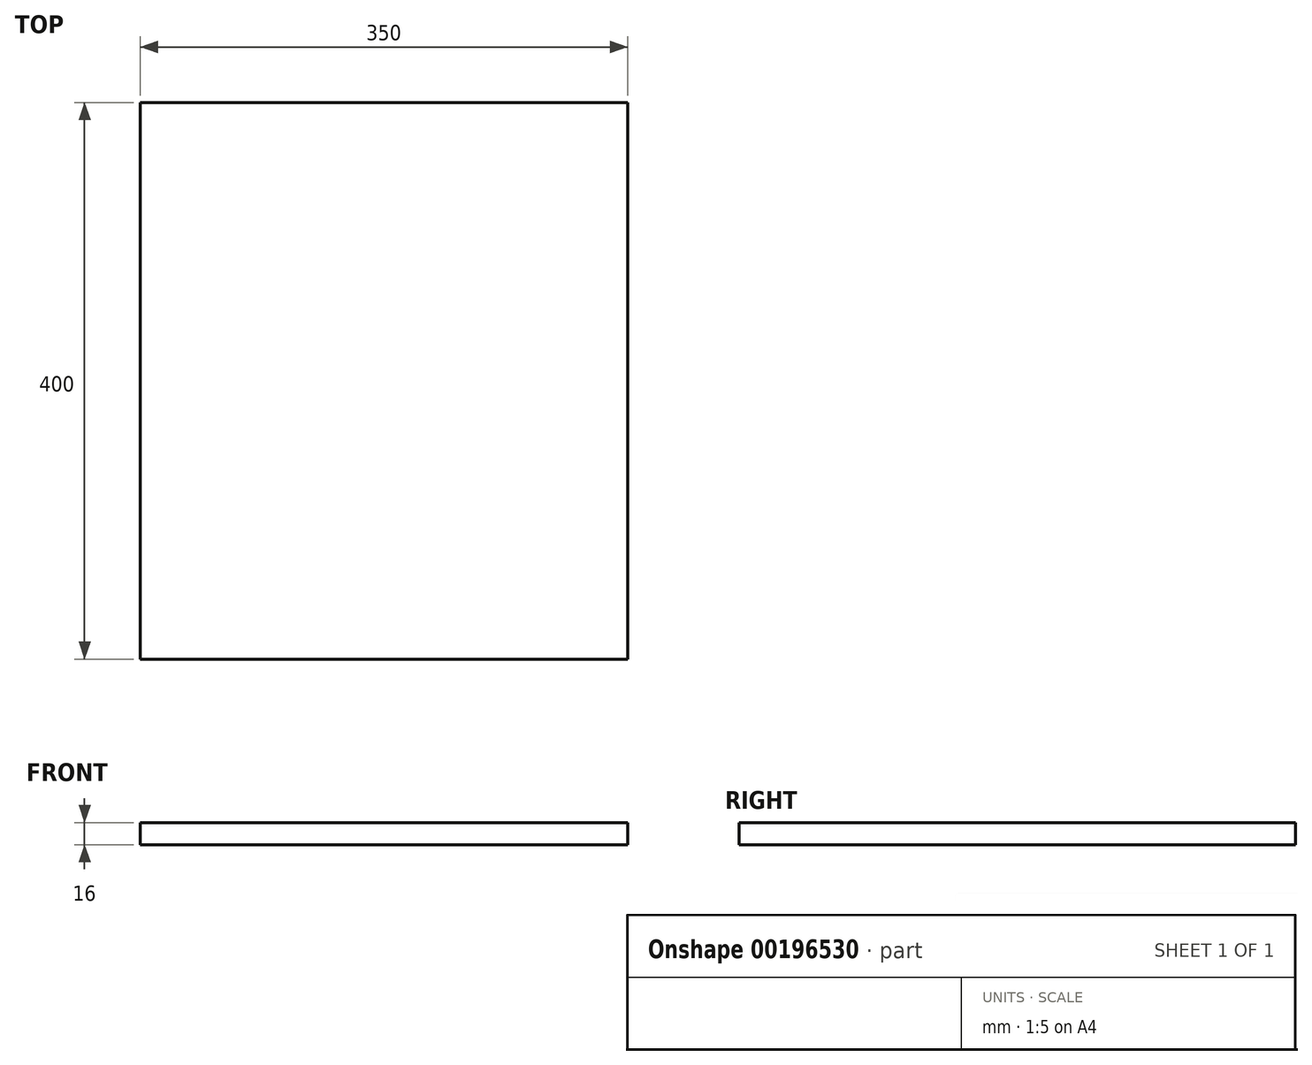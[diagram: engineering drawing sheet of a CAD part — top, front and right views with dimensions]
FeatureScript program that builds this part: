
annotation { "Feature Type Name" : "Feature", "Feature Type Description" : "" }
export const myFeature = defineFeature(function(context is Context, id is Id, definition is map)
    precondition{}
    {
        {
            var Q0;
            Q0=qCreatedBy(makeId("Top.planeOp"),FACE);
            var sketch = newSketch(context, id + "F0", { "sketchPlane" : qUnion([Q0])});
            skLineSegment(sketch, "E0.bottom", {"start": v(-864.34, -235.28) * mm, "end": v(-514.34, -235.28) * mm});
            skLineSegment(sketch, "E0.top", {"start": v(-864.34, 164.72) * mm, "end": v(-514.34, 164.72) * mm});
            skLineSegment(sketch, "E0.left", {"start": v(-864.34, -235.28) * mm, "end": v(-864.34, 164.72) * mm});
            skLineSegment(sketch, "E0.right", {"start": v(-514.34, -235.28) * mm, "end": v(-514.34, 164.72) * mm});
            skSolve(sketch);
        }
        {
            var Q0;
            Q0=makeQuery(id+"F0.imprint","IMPRINT",FACE,{"disambiguationData":[TD([[makeQuery(id+"F0.imprint","IMPRINT",EDGE,{"derivedFrom":sQuery(id+"F0.wireOp",EDGE,"E0.bottom")}),1.0]])]});
            extrude(context, id + "F1", {"entities" : qUnion([Q0]), "depth" : 16 * mm});
        }
    });
